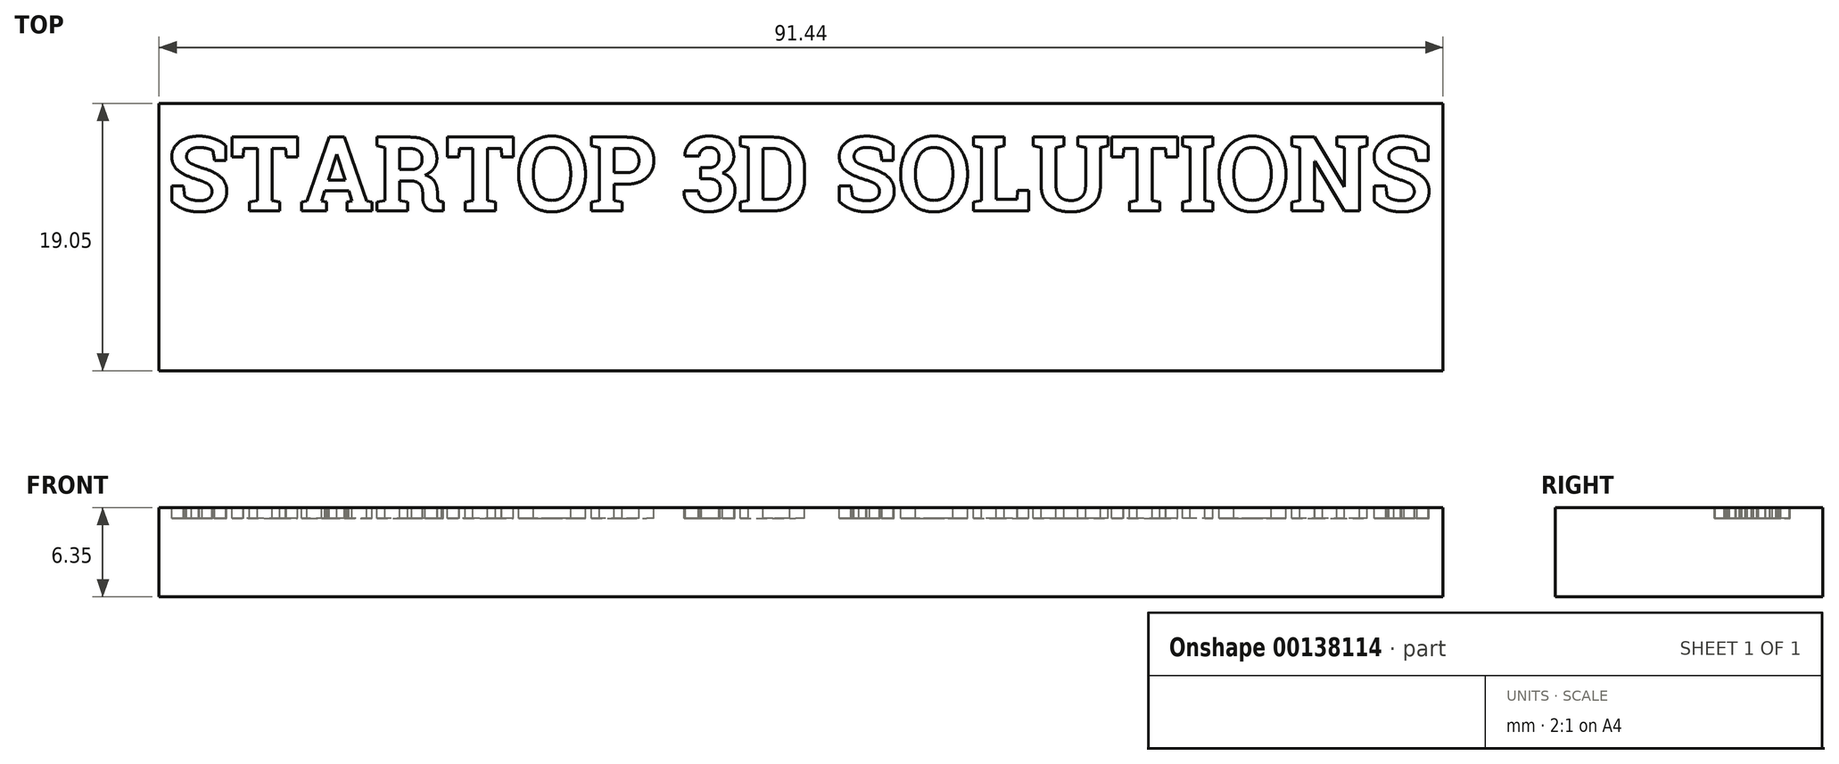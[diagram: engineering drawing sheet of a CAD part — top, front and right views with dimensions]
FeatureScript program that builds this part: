
annotation { "Feature Type Name" : "Feature", "Feature Type Description" : "" }
export const myFeature = defineFeature(function(context is Context, id is Id, definition is map)
    precondition{}
    {
        {
            var Q0;
            Q0=qCreatedBy(makeId("Top.planeOp"),FACE);
            var sketch = newSketch(context, id + "F0", { "sketchPlane" : qUnion([Q0])});
            skLineSegment(sketch, "E0.bottom", {"start": v(0, 0) * mm, "end": v(91.44, 0) * mm});
            skLineSegment(sketch, "E0.top", {"start": v(0, 19.05) * mm, "end": v(91.44, 19.05) * mm});
            skLineSegment(sketch, "E0.left", {"start": v(0, 0) * mm, "end": v(0, 19.05) * mm});
            skLineSegment(sketch, "E0.right", {"start": v(91.44, 0) * mm, "end": v(91.44, 19.05) * mm});
            skSolve(sketch);
        }
        {
            var Q0;
            Q0=qSketchRegion(id+"F0",true);
            extrude(context, id + "F1", {"entities" : qUnion([Q0]), "depth" : 6.35 * mm});
        }
        {
            var Q0;
            Q0=makeQuery(id+"F1.opExtrude","CAP_FACE",FACE,{"disambiguationData":[OSD([sQuery(id+"F0.wireOp",EDGE,"E0.bottom"),sQuery(id+"F0.wireOp",EDGE,"E0.top"),sQuery(id+"F0.wireOp",EDGE,"E0.left"),sQuery(id+"F0.wireOp",EDGE,"E0.right")])],"isStart":false});
            var sketch = newSketch(context, id + "F2", { "sketchPlane" : qUnion([Q0])});
            skLineSegment(sketch, "E1", {"start": v(0, 9.53) * mm, "end": v(91.44, 9.53) * mm, "construction": true});
            skText(sketch, "E2", { "text": "STARTOP 3D SOLUTIONS", "fontName": "RobotoSlab-Bold.ttf"});
            const initialGuessF2  = {"E2": [0.00056, 0.0114, 1, 0, 0.00532]};
            skSetInitialGuess(sketch, initialGuessF2);
            skSolve(sketch);
        }
        {
            var Q0;
            Q0=qSketchRegion(id+"F2",true);
            extrude(context, id + "F3", {"entities" : qUnion([Q0]), "operationType" : NewBodyOperationType.REMOVE, "oppositeDirection" : true, "depth" : 0.76 * mm});
        }
    });
